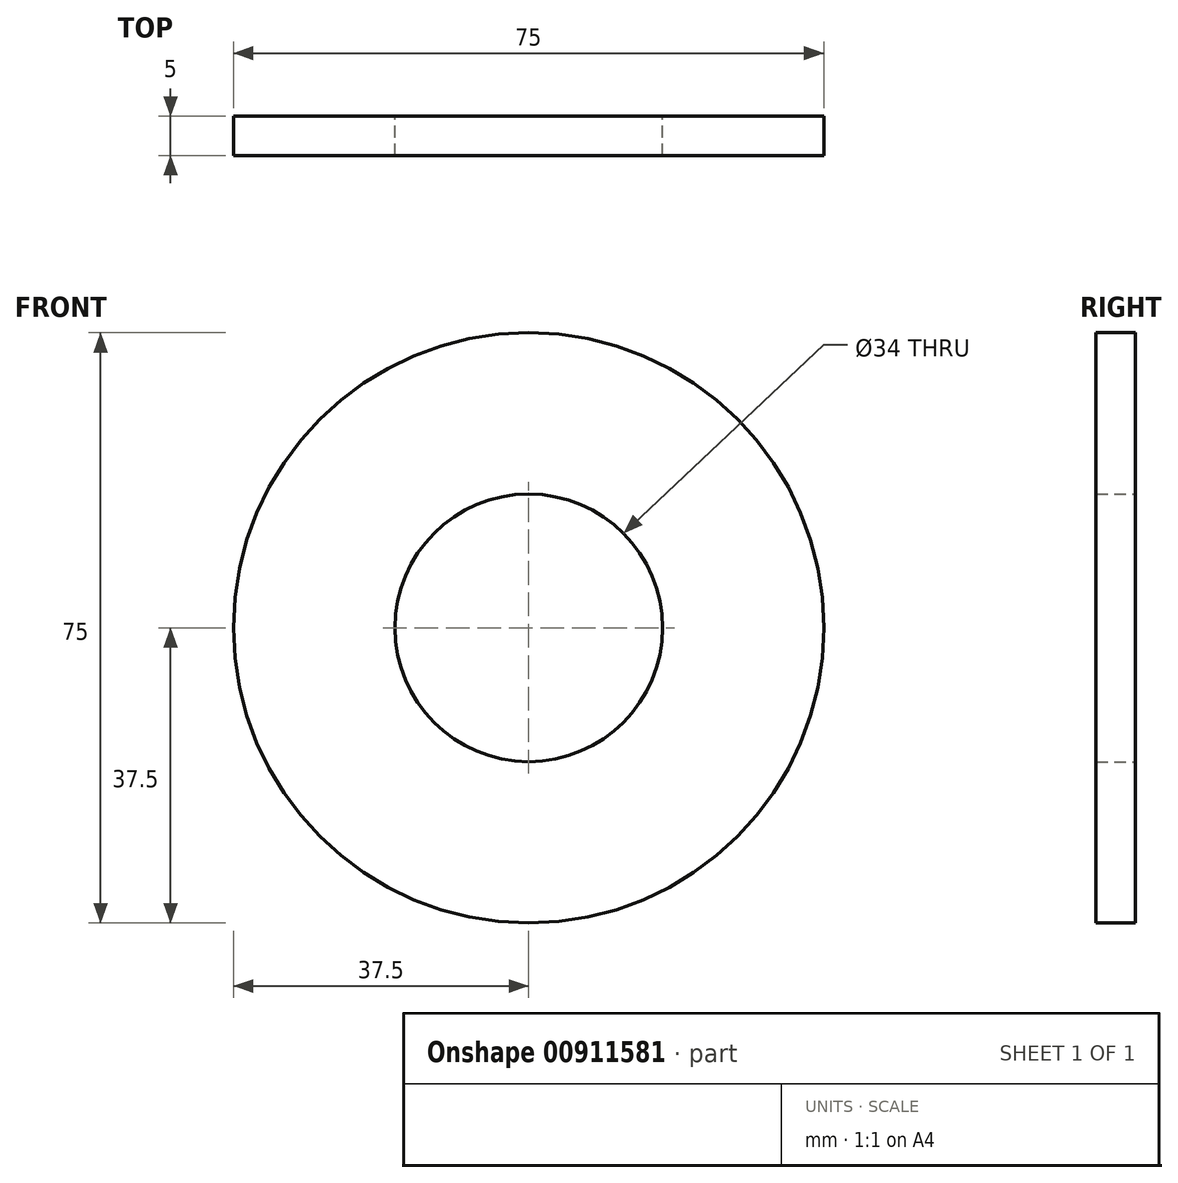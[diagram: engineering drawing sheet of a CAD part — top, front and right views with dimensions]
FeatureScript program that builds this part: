
annotation { "Feature Type Name" : "Feature", "Feature Type Description" : "" }
export const myFeature = defineFeature(function(context is Context, id is Id, definition is map)
    precondition{}
    {
        {
            var Q0;
            Q0=qCreatedBy(makeId("Front.planeOp"),FACE);
            var sketch = newSketch(context, id + "F0", { "sketchPlane" : qUnion([Q0])});
            skCircle(sketch, "E0", {"center": v(0, 0) * mm, "radius": 37.5 * mm});
            skCircle(sketch, "E1", {"center": v(0, 0) * mm, "radius": 17 * mm});
            skSolve(sketch);
        }
        {
            var Q0;
            Q0=makeQuery(id+"F0.imprint","IMPRINT",FACE,{"disambiguationData":[TD([[makeQuery(id+"F0.imprint","IMPRINT",EDGE,{"derivedFrom":sQuery(id+"F0.wireOp",EDGE,"E0")}),1.0]])]});
            extrude(context, id + "F1", {"entities" : qUnion([Q0]), "depth" : 5 * mm, "offsetDistance" : 25 * mm});
        }
        {
            var Q0;
            Q0=makeQuery(id+"F1.opExtrude","CAP_FACE",FACE,{"disambiguationData":[OSD([sQuery(id+"F0.wireOp",EDGE,"E0"),sQuery(id+"F0.wireOp",EDGE,"E1")])],"isStart":false});
            var sketch = newSketch(context, id + "F2", { "sketchPlane" : qUnion([Q0])});
            skCircle(sketch, "E2", {"center": v(0, 0) * mm, "radius": 17 * mm});
            skSolve(sketch);
        }
        {
            var Q0;
            Q0=sQuery(id+"F2.wireOp",EDGE,"E2");
            extrude(context, id + "F3", {"bodyType" : ToolBodyType.SURFACE, "surfaceEntities" : qUnion([Q0]), "depth" : 47.7 * mm, "offsetDistance" : 25 * mm});
        }
    });
